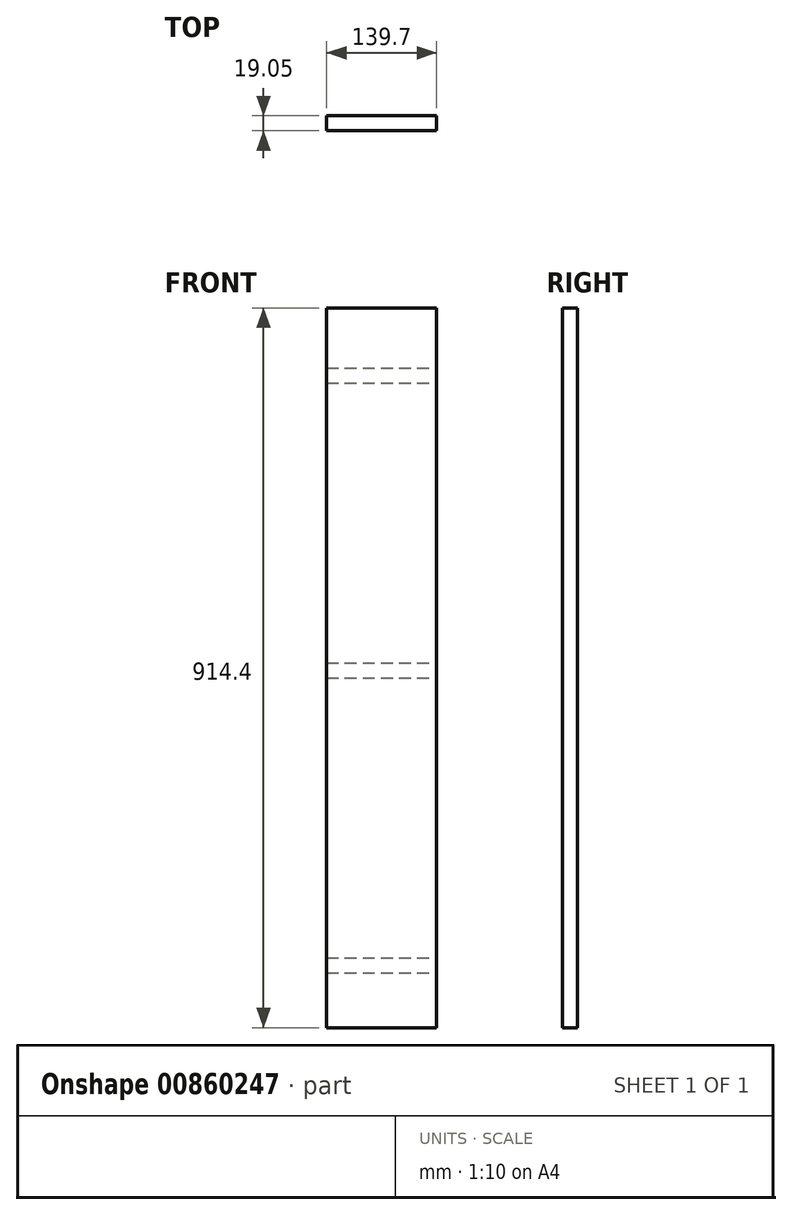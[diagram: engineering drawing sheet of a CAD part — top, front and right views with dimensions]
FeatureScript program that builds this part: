
annotation { "Feature Type Name" : "Feature", "Feature Type Description" : "" }
export const myFeature = defineFeature(function(context is Context, id is Id, definition is map)
    precondition{}
    {
        {
            var Q0;
            Q0=qCreatedBy(makeId("Front.planeOp"),FACE);
            var sketch = newSketch(context, id + "F0", { "sketchPlane" : qUnion([Q0])});
            skLineSegment(sketch, "E0.bottom", {"start": v(69.85, -457.2) * mm, "end": v(-69.85, -457.2) * mm});
            skLineSegment(sketch, "E0.top", {"start": v(69.85, 457.2) * mm, "end": v(-69.85, 457.2) * mm});
            skLineSegment(sketch, "E0.left", {"start": v(69.85, -457.2) * mm, "end": v(69.85, 457.2) * mm});
            skLineSegment(sketch, "E0.right", {"start": v(-69.85, -457.2) * mm, "end": v(-69.85, 457.2) * mm});
            skPoint(sketch, "E0.middle", {"position": v(0, 0) * mm});
            skSolve(sketch);
        }
        {
            var Q0;
            Q0 = qSketchRegion(id + "F0", true);
            extrude(context, id + "F1", {"entities" : qUnion([Q0]), "depth" : 19.05 * mm, "offsetDistance" : 25.4 * mm});
        }
        {
            var Q0;
            Q0=makeQuery(id+"F1.opExtrude","CAP_FACE",FACE,{"disambiguationData":[OSD([sQuery(id+"F0.wireOp",EDGE,"E0.bottom"),sQuery(id+"F0.wireOp",EDGE,"E0.top"),sQuery(id+"F0.wireOp",EDGE,"E0.left"),sQuery(id+"F0.wireOp",EDGE,"E0.right")])],"isStart":true});
            var sketch = newSketch(context, id + "F2", { "sketchPlane" : qUnion([Q0])});
            skLineSegment(sketch, "E1.bottom", {"start": v(69.85, 361.95) * mm, "end": v(-69.85, 361.95) * mm});
            skLineSegment(sketch, "E1.top", {"start": v(69.85, 381) * mm, "end": v(-69.85, 381) * mm});
            skLineSegment(sketch, "E1.left", {"start": v(69.85, 361.95) * mm, "end": v(69.85, 381) * mm});
            skLineSegment(sketch, "E1.right", {"start": v(-69.85, 361.95) * mm, "end": v(-69.85, 381) * mm});
            skPoint(sketch, "E1.middle", {"position": v(0, 371.48) * mm});
            skLineSegment(sketch, "E2.bottom", {"start": v(69.85, -12.7) * mm, "end": v(-69.85, -12.7) * mm});
            skLineSegment(sketch, "E2.top", {"start": v(69.85, 6.35) * mm, "end": v(-69.85, 6.35) * mm});
            skLineSegment(sketch, "E2.left", {"start": v(69.85, -12.7) * mm, "end": v(69.85, 6.35) * mm});
            skLineSegment(sketch, "E2.right", {"start": v(-69.85, -12.7) * mm, "end": v(-69.85, 6.35) * mm});
            skPoint(sketch, "E2.middle", {"position": v(0, -3.17) * mm});
            skLineSegment(sketch, "E3.bottom", {"start": v(69.85, -387.35) * mm, "end": v(-69.85, -387.35) * mm});
            skLineSegment(sketch, "E3.top", {"start": v(69.85, -368.3) * mm, "end": v(-69.85, -368.3) * mm});
            skLineSegment(sketch, "E3.left", {"start": v(69.85, -387.35) * mm, "end": v(69.85, -368.3) * mm});
            skLineSegment(sketch, "E3.right", {"start": v(-69.85, -387.35) * mm, "end": v(-69.85, -368.3) * mm});
            skPoint(sketch, "E3.middle", {"position": v(0, -377.82) * mm});
            skSolve(sketch);
        }
        {
            var Q0;
            Q0 = qSketchRegion(id + "F2", true);
            extrude(context, id + "F3", {"entities" : qUnion([Q0]), "operationType" : NewBodyOperationType.REMOVE, "oppositeDirection" : true, "depth" : 0.75 / 50.8 * mm, "offsetDistance" : 25.4 * mm});
        }
    });
